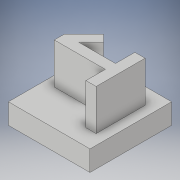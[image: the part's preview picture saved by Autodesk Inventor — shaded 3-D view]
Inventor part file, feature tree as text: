
AUTODESK INVENTOR PART (.ipt)
format: ipt  version: 2019 (Build 230136000, 136)  size: 119,808 bytes
history: native  units: mm
features: extrude x2, sketch x2
ambient origin geometry x8: Origin, YZ Plane, XZ Plane, XY Plane, X Axis, Y Axis, Z Axis, Center Point
bodies: Solid1 (feature_tree)
feature tree (4):
  extrude  "Extrusion1"  Depth=20.0mm
  extrude  "Extrusion2"  Depth=2.5mm
  sketch  "Sketch1"  dims[d0=20.0mm d1=20.0mm]
  sketch  "Sketch2"  dims[d2=5.0mm d3=0.0mm d13=2.5mm d14=2.5mm d15=2.5mm d16=2.5mm d17=3.0mm d18=12.0mm d19=2.5mm d20=2.5mm d21=45.0deg d22=10.0mm d23=0.0mm]
